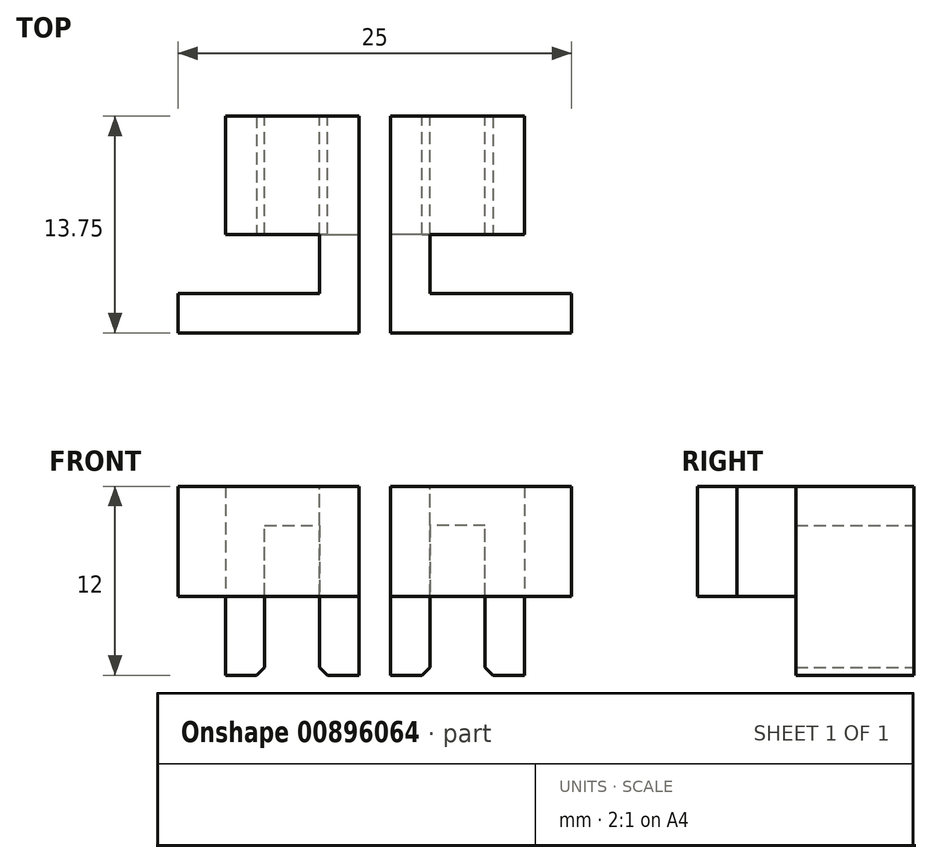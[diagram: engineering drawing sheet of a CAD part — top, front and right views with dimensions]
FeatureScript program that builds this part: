
annotation { "Feature Type Name" : "Feature", "Feature Type Description" : "" }
export const myFeature = defineFeature(function(context is Context, id is Id, definition is map)
    precondition{}
    {
        {
            var Q0;
            Q0=qCreatedBy(makeId("Front.planeOp"),FACE);
            var sketch = newSketch(context, id + "F0", { "sketchPlane" : qUnion([Q0])});
            skLineSegment(sketch, "E0", {"start": v(-7, 0) * mm, "end": v(-7, 9.5) * mm});
            skLineSegment(sketch, "E1", {"start": v(-7, 9.5) * mm, "end": v(-3.5, 9.5) * mm});
            skLineSegment(sketch, "E2", {"start": v(-3.5, 9.5) * mm, "end": v(-3.5, 0) * mm});
            skLineSegment(sketch, "E3", {"start": v(-3.5, 0) * mm, "end": v(-1, 0) * mm});
            skLineSegment(sketch, "E4", {"start": v(-1, 0) * mm, "end": v(-1, 12) * mm});
            skLineSegment(sketch, "E5", {"start": v(-1, 12) * mm, "end": v(-9.5, 12) * mm});
            skLineSegment(sketch, "E6", {"start": v(-9.5, 12) * mm, "end": v(-9.5, 0) * mm});
            skLineSegment(sketch, "E7", {"start": v(-9.5, 0) * mm, "end": v(-7, 0) * mm});
            skLineSegment(sketch, "E8", {"start": v(-5.25, 9.5) * mm, "end": v(-5.25, 12) * mm, "construction": true});
            skLineSegment(sketch, "E9", {"start": v(-7, 0) * mm, "end": v(-3.5, 0) * mm, "construction": true});
            skLineSegment(sketch, "E10", {"start": v(-5.25, 0) * mm, "end": v(-5.25, 9.5) * mm, "construction": true});
            skSolve(sketch);
        }
        {
            var Q0;
            Q0 = qSketchRegion(id + "F0", true);
            extrude(context, id + "F1", {"entities" : qUnion([Q0]), "endBound" : BoundingType.SYMMETRIC, "depth" : 7.5 * mm, "offsetDistance" : 25 * mm});
        }
        {
            var Q0;
            Q0=makeQuery(id+"F1.opExtrude","SWEPT_FACE",FACE,{"disambiguationData":[OSD([sQuery(id+"F0.wireOp",EDGE,"E5")])]});
            var sketch = newSketch(context, id + "F2", { "sketchPlane" : qUnion([Q0])});
            skLineSegment(sketch, "E11", {"start": v(-1, -3.75) * mm, "end": v(-1, -10) * mm});
            skLineSegment(sketch, "E12", {"start": v(-1, -10) * mm, "end": v(-12.5, -10) * mm});
            skLineSegment(sketch, "E13", {"start": v(-12.5, -10) * mm, "end": v(-12.5, -7.5) * mm});
            skLineSegment(sketch, "E14", {"start": v(-12.5, -7.5) * mm, "end": v(-3.5, -7.5) * mm});
            skLineSegment(sketch, "E15", {"start": v(-3.5, -7.5) * mm, "end": v(-3.5, -3.75) * mm});
            skLineSegment(sketch, "E16", {"start": v(-3.5, -3.75) * mm, "end": v(-1, -3.75) * mm});
            skPoint(sketch, "E17.0", {"position": v(-3.5, -3.75) * mm});
            skSolve(sketch);
        }
        {
            var Q0;
            Q0 = qSketchRegion(id + "F2", true);
            var Q1;
            Q1=makeQuery(id+"F1.opExtrude","SWEPT_FACE",FACE,{"disambiguationData":[OSD([sQuery(id+"F0.wireOp",EDGE,"E3")])]});
            extrude(context, id + "F3", {"entities" : qUnion([Q0]), "operationType" : NewBodyOperationType.ADD, "endBound" : BoundingType.UP_TO_SURFACE, "oppositeDirection" : true, "depth" : 25 * mm, "endBoundEntityFace" : qUnion([Q1]), "hasOffset" : true, "offsetDistance" : 5 * mm});
        }
        {
            var Q0;
            Q0=makeQuery(id+"F1.opExtrude","SWEPT_EDGE",EDGE,{"disambiguationData":[OSD([sQuery(id+"F0.wireOp",EDGE,"E2"),sQuery(id+"F0.wireOp",EDGE,"E3")])]});
            var Q1;
            Q1=makeQuery(id+"F1.opExtrude","SWEPT_EDGE",EDGE,{"disambiguationData":[OSD([sQuery(id+"F0.wireOp",EDGE,"E0"),sQuery(id+"F0.wireOp",EDGE,"E7")])]});
            chamfer(context, id + "F4", {"entities" : qUnion([Q0, Q1]), "width" : 0.5 * mm, "tangentPropagation" : true});
        }
        {
            var Q0;
            Q0=makeQuery(id+"F1.opExtrude","SWEPT_BODY",BODY,{"disambiguationData":[OSD([sQuery(id+"F0.wireOp",EDGE,"E0"),sQuery(id+"F0.wireOp",EDGE,"E1"),sQuery(id+"F0.wireOp",EDGE,"E2"),sQuery(id+"F0.wireOp",EDGE,"E3"),sQuery(id+"F0.wireOp",EDGE,"E4"),sQuery(id+"F0.wireOp",EDGE,"E5"),sQuery(id+"F0.wireOp",EDGE,"E6"),sQuery(id+"F0.wireOp",EDGE,"E7")])]});
            var Q1;
            Q1=qCreatedBy(makeId("Right.planeOp"),FACE);
            mirror(context, id + "F5", {"entities" : qUnion([Q0]), "mirrorPlane" : qUnion([Q1])});
        }
    });
